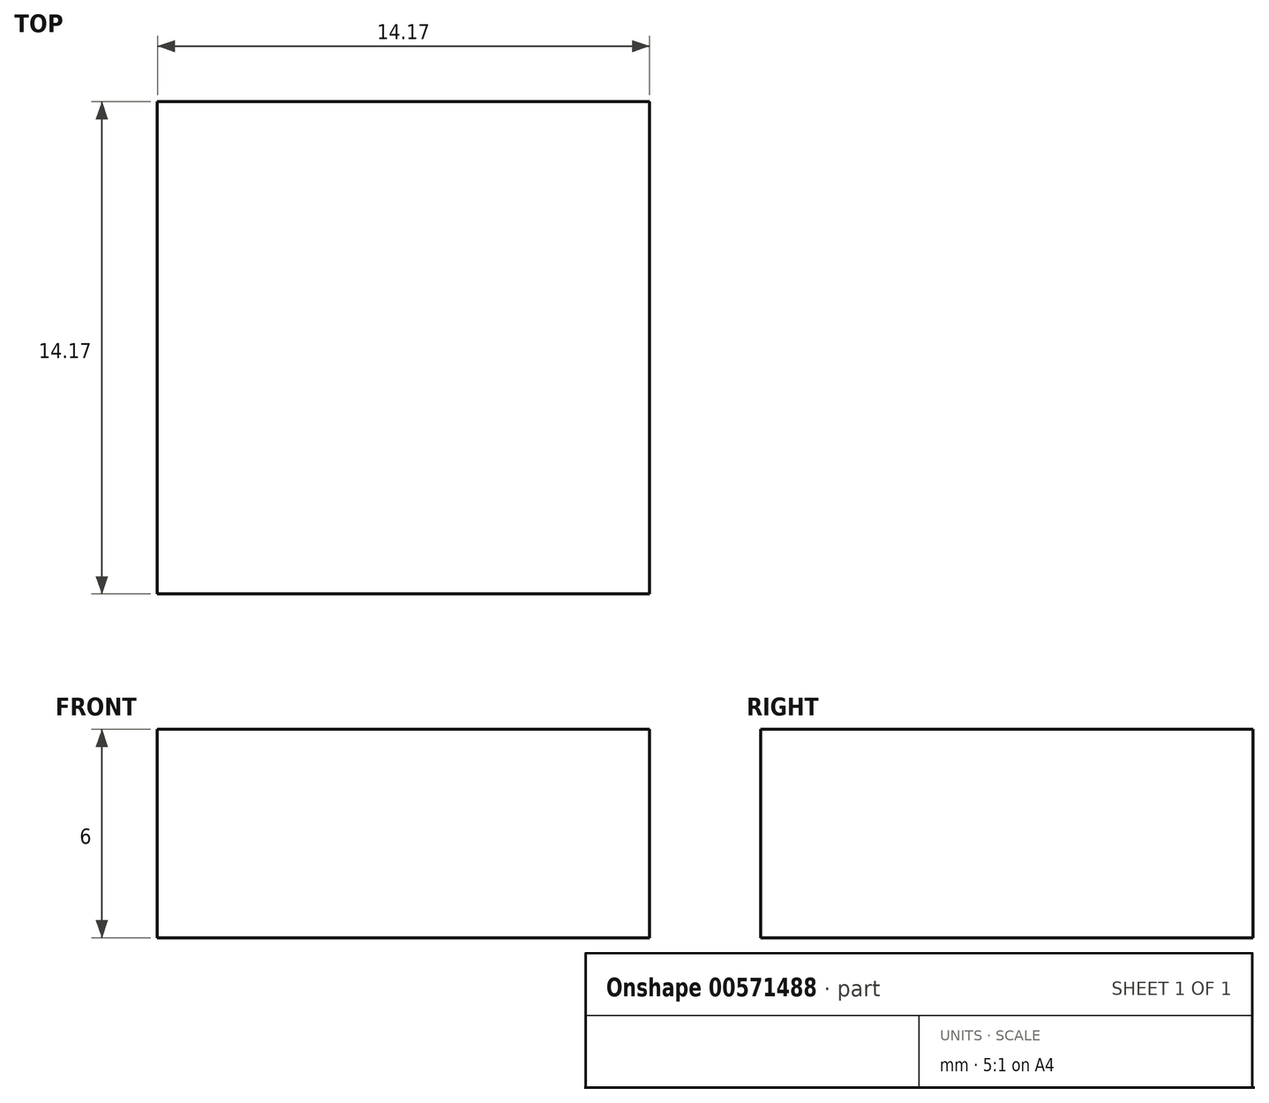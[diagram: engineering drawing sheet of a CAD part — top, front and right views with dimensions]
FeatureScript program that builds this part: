
annotation { "Feature Type Name" : "Feature", "Feature Type Description" : "" }
export const myFeature = defineFeature(function(context is Context, id is Id, definition is map)
    precondition{}
    {
        {
            var Q0;
            Q0=qCreatedBy(makeId("Top.planeOp"),FACE);
            var sketch = newSketch(context, id + "F0", { "sketchPlane" : qUnion([Q0])});
            skLineSegment(sketch, "E0.bottom", {"start": v(-26.13, 21.42) * mm, "end": v(-11.96, 21.42) * mm});
            skLineSegment(sketch, "E0.top", {"start": v(-26.13, 7.25) * mm, "end": v(-11.96, 7.25) * mm});
            skLineSegment(sketch, "E0.left", {"start": v(-26.13, 21.42) * mm, "end": v(-26.13, 7.25) * mm});
            skLineSegment(sketch, "E0.right", {"start": v(-11.96, 21.42) * mm, "end": v(-11.96, 7.25) * mm});
            skSolve(sketch);
        }
        {
            var Q0;
            Q0=makeQuery(id+"F0.imprint","IMPRINT",FACE,{"disambiguationData":[TD([[makeQuery(id+"F0.imprint","IMPRINT",EDGE,{"derivedFrom":sQuery(id+"F0.wireOp",EDGE,"E0.bottom")}),-1.0]])]});
            extrude(context, id + "F1", {"entities" : qUnion([Q0]), "depth" : 6 * mm, "offsetDistance" : 25 * mm});
        }
    });
